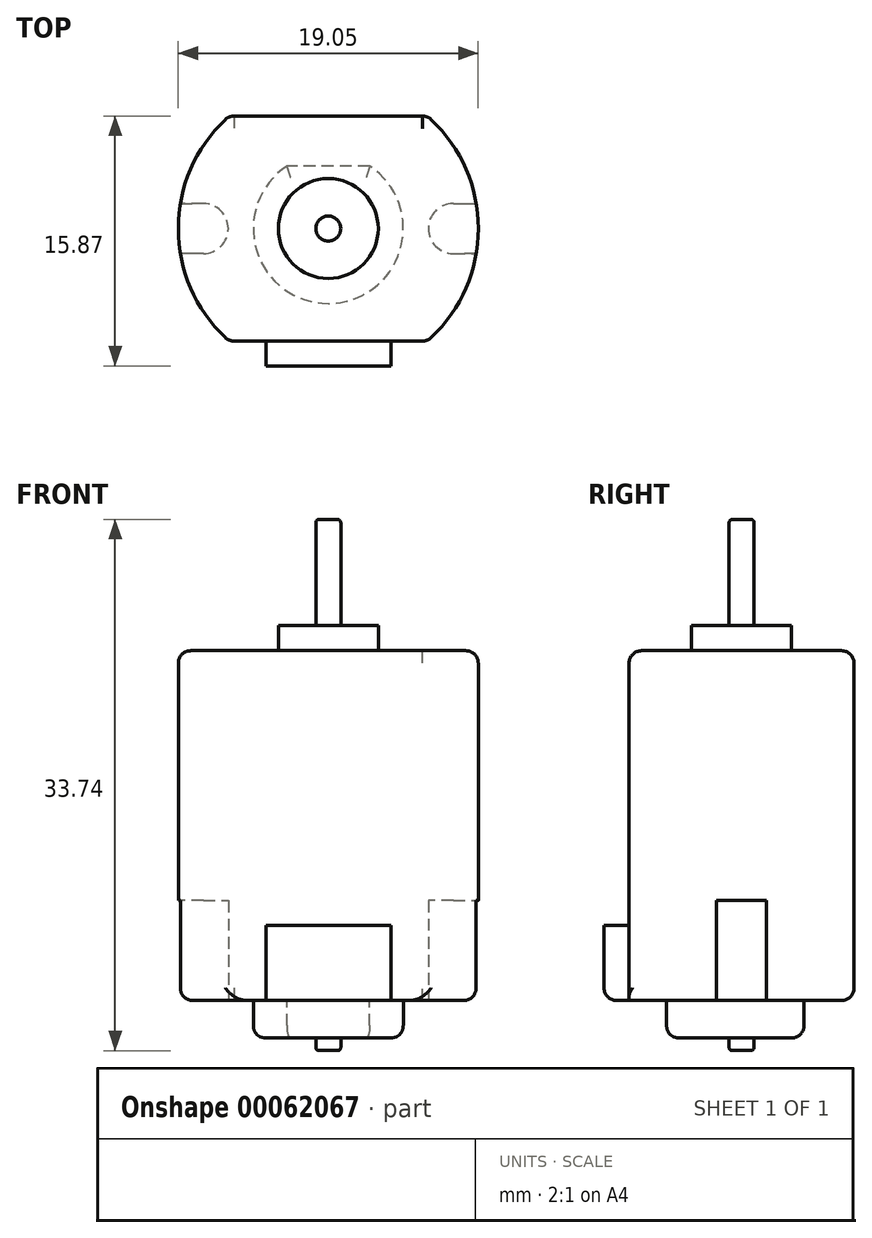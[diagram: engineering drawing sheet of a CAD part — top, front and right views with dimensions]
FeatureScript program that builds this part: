
annotation { "Feature Type Name" : "Feature", "Feature Type Description" : "" }
export const myFeature = defineFeature(function(context is Context, id is Id, definition is map)
    precondition{}
    {
        {
            var Q0;
            Q0=qCreatedBy(makeId("Top.planeOp"),FACE);
            var sketch = newSketch(context, id + "F0", { "sketchPlane" : qUnion([Q0])});
            skArc(sketch, "E0", {"start": v(-6.3, 7.14) * mm, "mid": v(-9.53, 0) * mm, "end": v(-6.3, -7.14) * mm});
            skLineSegment(sketch, "E1", {"start": v(0, 0) * mm, "end": v(0, -7.14) * mm, "construction": true});
            skLineSegment(sketch, "E2", {"start": v(0, 0) * mm, "end": v(0, 7.14) * mm, "construction": true});
            skLineSegment(sketch, "E3", {"start": v(6.3, 7.14) * mm, "end": v(-6.3, 7.14) * mm});
            skLineSegment(sketch, "E4", {"start": v(6.3, -7.14) * mm, "end": v(-6.3, -7.14) * mm});
            skArc(sketch, "E5.trimOffspring", {"start": v(6.3, -7.14) * mm, "mid": v(9.53, 0) * mm, "end": v(6.3, 7.14) * mm});
            skSolve(sketch);
        }
        {
            var Q0;
            Q0 = qSketchRegion(id + "F0", true);
            extrude(context, id + "F1", {"entities" : qUnion([Q0]), "depth" : 22.22 * mm});
        }
        {
            var Q0;
            Q0=makeQuery(id+"F1.opExtrude","CAP_FACE",FACE,{"disambiguationData":[OSD([sQuery(id+"F0.wireOp",EDGE,"E0"),sQuery(id+"F0.wireOp",EDGE,"E3"),sQuery(id+"F0.wireOp",EDGE,"E4"),sQuery(id+"F0.wireOp",EDGE,"E5.trimOffspring")])],"isStart":false});
            var sketch = newSketch(context, id + "F2", { "sketchPlane" : qUnion([Q0])});
            skCircle(sketch, "E6", {"center": v(0, 0) * mm, "radius": 3.17 * mm});
            skSolve(sketch);
        }
        {
            var Q0;
            Q0=makeQuery(id+"F2.imprint","IMPRINT",FACE,{"disambiguationData":[TD([[makeQuery(id+"F2.imprint","IMPRINT",EDGE,{"derivedFrom":sQuery(id+"F2.wireOp",EDGE,"E6")}),1.0]])]});
            extrude(context, id + "F3", {"entities" : qUnion([Q0]), "operationType" : NewBodyOperationType.ADD, "depth" : 1.59 * mm});
        }
        {
            var Q0;
            Q0=makeQuery(id+"F3.opExtrude","CAP_FACE",FACE,{"disambiguationData":[OSD([sQuery(id+"F2.wireOp",EDGE,"E6")])],"isStart":false});
            var sketch = newSketch(context, id + "F4", { "sketchPlane" : qUnion([Q0])});
            skCircle(sketch, "E7", {"center": v(0, 0) * mm, "radius": 0.8 * mm});
            skSolve(sketch);
        }
        {
            var Q0;
            Q0 = qSketchRegion(id + "F4", true);
            extrude(context, id + "F5", {"entities" : qUnion([Q0]), "operationType" : NewBodyOperationType.ADD, "depth" : 6.75 * mm});
        }
        {
            var Q0;
            Q0=makeQuery(id+"F1.opExtrude","CAP_FACE",FACE,{"disambiguationData":[OSD([sQuery(id+"F0.wireOp",EDGE,"E0"),sQuery(id+"F0.wireOp",EDGE,"E3"),sQuery(id+"F0.wireOp",EDGE,"E4"),sQuery(id+"F0.wireOp",EDGE,"E5.trimOffspring")])],"isStart":true});
            var sketch = newSketch(context, id + "F6", { "sketchPlane" : qUnion([Q0])});
            skLineSegment(sketch, "E8", {"start": v(-9.53, 0) * mm, "end": v(-6.35, 0) * mm, "construction": true});
            skPoint(sketch, "E8.endSnap0", {"position": v(-9.53, 0) * mm});
            skLineSegment(sketch, "E9", {"start": v(-7.94, 0) * mm, "end": v(-7.94, 1.59) * mm, "construction": true});
            skLineSegment(sketch, "E10", {"start": v(-7.94, 0) * mm, "end": v(-7.94, -1.59) * mm, "construction": true});
            skLineSegment(sketch, "E11", {"start": v(9.53, 0) * mm, "end": v(6.35, 0) * mm, "construction": true});
            skPoint(sketch, "E11.endSnap0", {"position": v(9.53, 0) * mm});
            skLineSegment(sketch, "E12", {"start": v(7.94, 0) * mm, "end": v(7.94, 1.59) * mm, "construction": true});
            skLineSegment(sketch, "E13", {"start": v(7.94, 0) * mm, "end": v(7.94, -1.59) * mm, "construction": true});
            skArc(sketch, "E14", {"start": v(-7.94, -1.59) * mm, "mid": v(-6.35, 0) * mm, "end": v(-7.94, 1.59) * mm});
            skArc(sketch, "E15", {"start": v(7.94, 1.59) * mm, "mid": v(6.35, 0) * mm, "end": v(7.94, -1.59) * mm});
            skLineSegment(sketch, "E16", {"start": v(-7.94, 1.59) * mm, "end": v(-9.4, 1.59) * mm});
            skLineSegment(sketch, "E17", {"start": v(-7.94, -1.59) * mm, "end": v(-9.4, -1.59) * mm});
            skLineSegment(sketch, "E18", {"start": v(7.94, 1.59) * mm, "end": v(9.4, 1.59) * mm});
            skLineSegment(sketch, "E19", {"start": v(7.94, -1.59) * mm, "end": v(9.4, -1.59) * mm});
            skSolve(sketch);
        }
        {
            var Q0;
            Q0=makeQuery(id+"F6.imprint","IMPRINT",FACE,{"disambiguationData":[TD([[makeQuery(id+"F6.imprint","IMPRINT",EDGE,{"derivedFrom":sQuery(id+"F6.wireOp",EDGE,"E14")}),1.0]])]});
            var Q1;
            Q1=makeQuery(id+"F6.imprint","IMPRINT",FACE,{"disambiguationData":[TD([[makeQuery(id+"F6.imprint","IMPRINT",EDGE,{"derivedFrom":sQuery(id+"F6.wireOp",EDGE,"E15")}),1.0]])]});
            extrude(context, id + "F7", {"entities" : qUnion([Q0, Q1]), "operationType" : NewBodyOperationType.REMOVE, "oppositeDirection" : true, "depth" : 6.35 * mm});
        }
        {
            var Q0;
            Q0=makeQuery(id+"F1.opExtrude","CAP_FACE",FACE,{"disambiguationData":[OSD([sQuery(id+"F0.wireOp",EDGE,"E0"),sQuery(id+"F0.wireOp",EDGE,"E3"),sQuery(id+"F0.wireOp",EDGE,"E4"),sQuery(id+"F0.wireOp",EDGE,"E5.trimOffspring")])],"isStart":true});
            var sketch = newSketch(context, id + "F8", { "sketchPlane" : qUnion([Q0])});
            skArc(sketch, "E20", {"start": v(2.63, -3.97) * mm, "mid": v(0, 4.76) * mm, "end": v(-2.63, -3.97) * mm});
            skLineSegment(sketch, "E21", {"start": v(0, 0) * mm, "end": v(0, -3.97) * mm, "construction": true});
            skLineSegment(sketch, "E22", {"start": v(2.63, -3.97) * mm, "end": v(-2.63, -3.97) * mm});
            skSolve(sketch);
        }
        {
            var Q0;
            Q0 = qSketchRegion(id + "F8", true);
            extrude(context, id + "F9", {"entities" : qUnion([Q0]), "operationType" : NewBodyOperationType.ADD, "depth" : 2.38 * mm});
        }
        {
            var Q0;
            Q0=makeQuery(id+"F9.opExtrude","CAP_FACE",FACE,{"disambiguationData":[OSD([sQuery(id+"F8.wireOp",EDGE,"E20"),sQuery(id+"F8.wireOp",EDGE,"E22")])],"isStart":false});
            var sketch = newSketch(context, id + "F10", { "sketchPlane" : qUnion([Q0])});
            skCircle(sketch, "E23", {"center": v(0, 0) * mm, "radius": 0.8 * mm});
            skSolve(sketch);
        }
        {
            var Q0;
            Q0 = qSketchRegion(id + "F10", true);
            extrude(context, id + "F11", {"entities" : qUnion([Q0]), "operationType" : NewBodyOperationType.ADD, "depth" : 0.8 * mm});
        }
        {
            var Q0;
            Q0=makeQuery(id+"F11.opExtrude","CAP_EDGE",EDGE,{"disambiguationData":[OSD([sQuery(id+"F10.wireOp",EDGE,"E23")])],"isStart":false});
            var Q1;
            Q1=makeQuery(id+"F5.opExtrude","CAP_EDGE",EDGE,{"disambiguationData":[OSD([sQuery(id+"F4.wireOp",EDGE,"E7")])],"isStart":false});
            fillet(context, id + "F12", {"entities" : qUnion([Q0, Q1]), "radius" : 0.2 * mm, "tangentPropagation" : true, "allowEdgeOverflow" : false});
        }
        {
            var Q0;
            Q0=makeQuery(id+"F1.opExtrude","SWEPT_FACE",FACE,{"disambiguationData":[OSD([sQuery(id+"F0.wireOp",EDGE,"E4")])]});
            var sketch = newSketch(context, id + "F13", { "sketchPlane" : qUnion([Q0])});
            skLineSegment(sketch, "E24", {"start": v(0, 0) * mm, "end": v(0, 4.76) * mm, "construction": true});
            skLineSegment(sketch, "E25", {"start": v(0, 4.76) * mm, "end": v(-3.97, 4.76) * mm, "construction": true});
            skLineSegment(sketch, "E26", {"start": v(0, 4.76) * mm, "end": v(3.97, 4.76) * mm, "construction": true});
            skLineSegment(sketch, "E27", {"start": v(-3.97, 4.76) * mm, "end": v(3.97, 4.76) * mm});
            skLineSegment(sketch, "E28", {"start": v(-3.97, 4.76) * mm, "end": v(-3.97, 0) * mm});
            skLineSegment(sketch, "E29", {"start": v(-3.97, 0) * mm, "end": v(3.97, 0) * mm});
            skLineSegment(sketch, "E30", {"start": v(3.97, 0) * mm, "end": v(3.97, 4.76) * mm});
            skSolve(sketch);
        }
        {
            var Q0;
            Q0 = qSketchRegion(id + "F13", true);
            extrude(context, id + "F14", {"entities" : qUnion([Q0]), "operationType" : NewBodyOperationType.ADD, "depth" : 1.59 * mm});
        }
        {
            var Q0;
            Q0=makeQuery(id+"F1.opExtrude","SWEPT_EDGE",EDGE,{"disambiguationData":[OSD([sQuery(id+"F0.wireOp",EDGE,"E3"),sQuery(id+"F0.wireOp",EDGE,"E5.trimOffspring")])]});
            var Q1;
            Q1=makeQuery(id+"F1.opExtrude","SWEPT_EDGE",EDGE,{"disambiguationData":[OSD([sQuery(id+"F0.wireOp",EDGE,"E0"),sQuery(id+"F0.wireOp",EDGE,"E3")])]});
            var Q2;
            Q2=makeQuery(id+"F1.opExtrude","SWEPT_EDGE",EDGE,{"disambiguationData":[OSD([sQuery(id+"F0.wireOp",EDGE,"E0"),sQuery(id+"F0.wireOp",EDGE,"E4")])]});
            var Q3;
            Q3=makeQuery(id+"F1.opExtrude","SWEPT_EDGE",EDGE,{"disambiguationData":[OSD([sQuery(id+"F0.wireOp",EDGE,"E4"),sQuery(id+"F0.wireOp",EDGE,"E5.trimOffspring")])]});
            var Q4;
            Q4=makeQuery(id+"F1.opExtrude","CAP_EDGE",EDGE,{"disambiguationData":[OSD([sQuery(id+"F0.wireOp",EDGE,"E4")])],"isStart":false});
            var Q5;
            Q5=makeQuery(id+"F1.opExtrude","CAP_EDGE",EDGE,{"disambiguationData":[OSD([sQuery(id+"F0.wireOp",EDGE,"E3")])],"isStart":false});
            var Q6;
            Q6=makeQuery(id+"F1.opExtrude","CAP_EDGE",EDGE,{"disambiguationData":[OSD([sQuery(id+"F0.wireOp",EDGE,"E3")])],"isStart":true});
            var Q7;
            Q7=makeQuery(id+"F9.opExtrude","CAP_EDGE",EDGE,{"disambiguationData":[OSD([sQuery(id+"F8.wireOp",EDGE,"E22")])],"isStart":false});
            var Q8;
            Q8=makeQuery(id+"F9.opExtrude","CAP_EDGE",EDGE,{"disambiguationData":[OSD([sQuery(id+"F8.wireOp",EDGE,"E20")])],"isStart":false});
            var Q9;
            Q9=makeQuery(id+"F7.boolean.opBoolean","COPY",EDGE,{"derivedFrom":makeQuery(id+"F7.opExtrude","CAP_EDGE",EDGE,{"disambiguationData":[OSD([sQuery(id+"F0.wireOp",EDGE,"E5.trimOffspring")])],"isStart":false})});
            var Q10;
            Q10=makeQuery(id+"F7.boolean.opBoolean","COPY",EDGE,{"derivedFrom":makeQuery(id+"F7.opExtrude","SWEPT_EDGE",EDGE,{"disambiguationData":[OSD([sQuery(id+"F0.wireOp",EDGE,"E5.trimOffspring"),sQuery(id+"F6.wireOp",EDGE,"E19")])]})});
            var Q11;
            Q11=makeQuery(id+"F7.boolean.opBoolean","COPY",EDGE,{"derivedFrom":makeQuery(id+"F7.opExtrude","SWEPT_EDGE",EDGE,{"disambiguationData":[OSD([sQuery(id+"F0.wireOp",EDGE,"E5.trimOffspring"),sQuery(id+"F6.wireOp",EDGE,"E18")])]})});
            var Q12;
            Q12=makeQuery(id+"F7.boolean.opBoolean","COPY",EDGE,{"derivedFrom":makeQuery(id+"F7.opExtrude","CAP_EDGE",EDGE,{"disambiguationData":[OSD([sQuery(id+"F6.wireOp",EDGE,"E15")])],"isStart":true})});
            var Q13;
            Q13=makeQuery(id+"F7.boolean.opBoolean","COPY",EDGE,{"derivedFrom":makeQuery(id+"F7.opExtrude","CAP_EDGE",EDGE,{"disambiguationData":[OSD([sQuery(id+"F0.wireOp",EDGE,"E0")])],"isStart":false})});
            var Q14;
            Q14=makeQuery(id+"F7.boolean.opBoolean","COPY",EDGE,{"derivedFrom":makeQuery(id+"F7.opExtrude","SWEPT_EDGE",EDGE,{"disambiguationData":[OSD([sQuery(id+"F0.wireOp",EDGE,"E0"),sQuery(id+"F6.wireOp",EDGE,"E17")])]})});
            var Q15;
            Q15=makeQuery(id+"F7.boolean.opBoolean","COPY",EDGE,{"derivedFrom":makeQuery(id+"F7.opExtrude","SWEPT_EDGE",EDGE,{"disambiguationData":[OSD([sQuery(id+"F0.wireOp",EDGE,"E0"),sQuery(id+"F6.wireOp",EDGE,"E16")])]})});
            var Q16;
            Q16=makeQuery(id+"F7.boolean.opBoolean","COPY",EDGE,{"derivedFrom":makeQuery(id+"F7.opExtrude","CAP_EDGE",EDGE,{"disambiguationData":[OSD([sQuery(id+"F6.wireOp",EDGE,"E14")])],"isStart":true})});
            var Q17;
            Q17=makeQuery(id+"F1.opExtrude","CAP_EDGE",EDGE,{"disambiguationData":[OSD([sQuery(id+"F0.wireOp",EDGE,"E5.trimOffspring")])],"isStart":false});
            var Q18;
            Q18=makeQuery(id+"F1.opExtrude","CAP_EDGE",EDGE,{"disambiguationData":[OSD([sQuery(id+"F0.wireOp",EDGE,"E0")])],"isStart":false});
            var Q19;
            {var subQ0=sQuery(id+"F0.wireOp",EDGE,"E5.trimOffspring");var subQ1=sQuery(id+"F0.wireOp",EDGE,"E4");Q19=makeQuery(id+"F7.boolean.opBoolean","SPLIT",EDGE,{"disambiguationData":[TD([makeQuery(id+"F1.opExtrude","SWEPT_FACE",FACE,{"disambiguationData":[OSD([subQ1])]})])],"derivedFrom":makeQuery(id+"F1.opExtrude","CAP_EDGE",EDGE,{"disambiguationData":[OSD([subQ0])],"isStart":true})});}
            var Q20;
            {var subQ0=sQuery(id+"F0.wireOp",EDGE,"E5.trimOffspring");var subQ1=sQuery(id+"F0.wireOp",EDGE,"E3");Q20=makeQuery(id+"F7.boolean.opBoolean","SPLIT",EDGE,{"disambiguationData":[TD([makeQuery(id+"F1.opExtrude","SWEPT_FACE",FACE,{"disambiguationData":[OSD([subQ1])]})])],"derivedFrom":makeQuery(id+"F1.opExtrude","CAP_EDGE",EDGE,{"disambiguationData":[OSD([subQ0])],"isStart":true})});}
            var Q21;
            {var subQ0=sQuery(id+"F0.wireOp",EDGE,"E0");var subQ1=sQuery(id+"F0.wireOp",EDGE,"E3");Q21=makeQuery(id+"F7.boolean.opBoolean","SPLIT",EDGE,{"disambiguationData":[TD([makeQuery(id+"F1.opExtrude","SWEPT_FACE",FACE,{"disambiguationData":[OSD([subQ1])]})])],"derivedFrom":makeQuery(id+"F1.opExtrude","CAP_EDGE",EDGE,{"disambiguationData":[OSD([subQ0])],"isStart":true})});}
            var Q22;
            {var subQ0=sQuery(id+"F0.wireOp",EDGE,"E0");var subQ1=sQuery(id+"F0.wireOp",EDGE,"E4");Q22=makeQuery(id+"F7.boolean.opBoolean","SPLIT",EDGE,{"disambiguationData":[TD([makeQuery(id+"F1.opExtrude","SWEPT_FACE",FACE,{"disambiguationData":[OSD([subQ1])]})])],"derivedFrom":makeQuery(id+"F1.opExtrude","CAP_EDGE",EDGE,{"disambiguationData":[OSD([subQ0])],"isStart":true})});}
            var Q23;
            Q23=makeQuery(id+"F14.opExtrude","CAP_EDGE",EDGE,{"disambiguationData":[OSD([sQuery(id+"F13.wireOp",EDGE,"E29")])],"isStart":false});
            fillet(context, id + "F15", {"entities" : qUnion([Q0, Q1, Q2, Q3, Q4, Q5, Q6, Q7, Q8, Q9, Q10, Q11, Q12, Q13, Q14, Q15, Q16, Q17, Q18, Q19, Q20, Q21, Q22, Q23]), "radius" : 0.8 * mm, "tangentPropagation" : true, "allowEdgeOverflow" : false});
        }
    });
